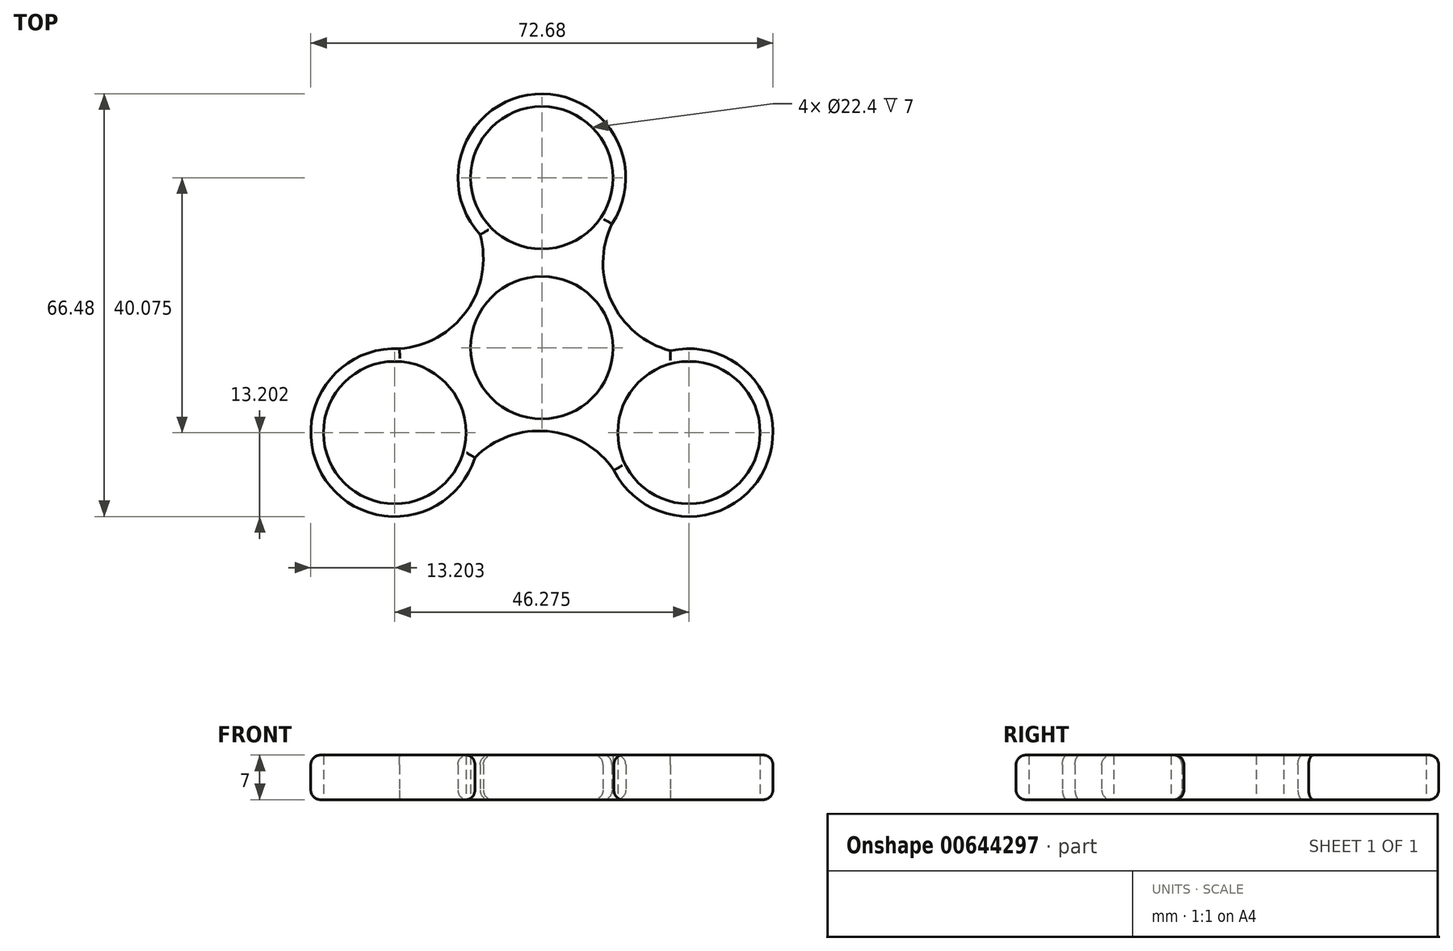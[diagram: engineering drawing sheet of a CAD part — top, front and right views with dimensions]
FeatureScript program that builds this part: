
annotation { "Feature Type Name" : "Feature", "Feature Type Description" : "" }
export const myFeature = defineFeature(function(context is Context, id is Id, definition is map)
    precondition{}
    {
        {
            var Q0;
            Q0=qCreatedBy(makeId("Top.planeOp"),FACE);
            var sketch = newSketch(context, id + "F0", { "sketchPlane" : qUnion([Q0])});
            skCircle(sketch, "E0", {"center": v(0, 0) * mm, "radius": 11.2 * mm});
            skArc(sketch, "E1", {"start": v(-10.62, 7.84) * mm, "mid": v(-11.33, 6.77) * mm, "end": v(-11.93, 5.65) * mm});
            skCircle(sketch, "E2", {"center": v(0, 26.72) * mm, "radius": 11.2 * mm});
            skArc(sketch, "E3", {"start": v(11.03, 19.46) * mm, "mid": v(-1.07, 39.87) * mm, "end": v(-9.7, 17.77) * mm});
            skCircle(sketch, "E4.1.0", {"center": v(-23.14, -13.36) * mm, "radius": 11.2 * mm});
            skArc(sketch, "E4.1.1", {"start": v(-22.36, -0.18) * mm, "mid": v(-34, -20.86) * mm, "end": v(-10.54, -17.3) * mm});
            skCircle(sketch, "E4.2.0", {"center": v(23.14, -13.36) * mm, "radius": 11.2 * mm});
            skArc(sketch, "E4.2.1", {"start": v(11.34, -19.28) * mm, "mid": v(35.07, -19) * mm, "end": v(20.24, -0.48) * mm});
            skArc(sketch, "E5", {"start": v(11.03, 19.46) * mm, "mid": v(10.94, 7.32) * mm, "end": v(20.24, -0.48) * mm});
            skArc(sketch, "E6.1.0", {"start": v(-22.36, -0.18) * mm, "mid": v(-11.8, 5.82) * mm, "end": v(-9.7, 17.77) * mm});
            skArc(sketch, "E6.2.0", {"start": v(11.34, -19.28) * mm, "mid": v(0.87, -13.14) * mm, "end": v(-10.54, -17.3) * mm});
            skArc(sketch, "E7.trimOffspring", {"start": v(12.1, 5.28) * mm, "mid": v(11.53, 6.42) * mm, "end": v(10.86, 7.5) * mm});
            skArc(sketch, "E8.trimOffspring", {"start": v(-1.48, -13.12) * mm, "mid": v(-0.2, -13.2) * mm, "end": v(1.08, -13.16) * mm});
            skLineSegment(sketch, "E9", {"start": v(-48.96, -28.96) * mm, "end": v(42.62, -28.96) * mm, "construction": true});
            skSolve(sketch);
        }
        {
            var Q0;
            Q0=makeQuery(id+"F0.imprint","IMPRINT",FACE,{"disambiguationData":[TD([[makeQuery(id+"F0.imprint","IMPRINT",EDGE,{"derivedFrom":sQuery(id+"F0.wireOp",EDGE,"E0")}),-1.0]])]});
            extrude(context, id + "F1", {"entities" : qUnion([Q0]), "depth" : 7 * mm, "offsetDistance" : 25 * mm});
        }
        {
            var Q0;
            Q0=makeQuery(id+"F1.opExtrude","CAP_EDGE",EDGE,{"disambiguationData":[OSD([sQuery(id+"F0.wireOp",EDGE,"E4.2.1")])],"isStart":false});
            var Q1;
            Q1=makeQuery(id+"F1.opExtrude","CAP_EDGE",EDGE,{"disambiguationData":[OSD([sQuery(id+"F0.wireOp",EDGE,"E5")])],"isStart":false});
            var Q2;
            Q2=makeQuery(id+"F1.opExtrude","CAP_EDGE",EDGE,{"disambiguationData":[OSD([sQuery(id+"F0.wireOp",EDGE,"E6.2.0")])],"isStart":false});
            var Q3;
            Q3=makeQuery(id+"F1.opExtrude","CAP_EDGE",EDGE,{"disambiguationData":[OSD([sQuery(id+"F0.wireOp",EDGE,"E4.1.1")])],"isStart":false});
            var Q4;
            Q4=makeQuery(id+"F1.opExtrude","CAP_EDGE",EDGE,{"disambiguationData":[OSD([sQuery(id+"F0.wireOp",EDGE,"E6.1.0")])],"isStart":false});
            var Q5;
            Q5=makeQuery(id+"F1.opExtrude","CAP_EDGE",EDGE,{"disambiguationData":[OSD([sQuery(id+"F0.wireOp",EDGE,"E3")])],"isStart":false});
            fillet(context, id + "F2", {"entities" : qUnion([Q0, Q1, Q2, Q3, Q4, Q5]), "tangentPropagation" : true, "radius" : 1.5 * mm, "defaultsChanged" : false, "vertexSettings" : [], "allowEdgeOverflow" : false});
        }
        {
            var Q0;
            Q0=makeQuery(id+"F1.opExtrude","CAP_EDGE",EDGE,{"disambiguationData":[OSD([sQuery(id+"F0.wireOp",EDGE,"E4.2.1")])],"isStart":true});
            var Q1;
            Q1=makeQuery(id+"F1.opExtrude","CAP_EDGE",EDGE,{"disambiguationData":[OSD([sQuery(id+"F0.wireOp",EDGE,"E5")])],"isStart":true});
            var Q2;
            Q2=makeQuery(id+"F1.opExtrude","CAP_EDGE",EDGE,{"disambiguationData":[OSD([sQuery(id+"F0.wireOp",EDGE,"E6.2.0")])],"isStart":true});
            var Q3;
            Q3=makeQuery(id+"F1.opExtrude","CAP_EDGE",EDGE,{"disambiguationData":[OSD([sQuery(id+"F0.wireOp",EDGE,"E4.1.1")])],"isStart":true});
            var Q4;
            Q4=makeQuery(id+"F1.opExtrude","CAP_EDGE",EDGE,{"disambiguationData":[OSD([sQuery(id+"F0.wireOp",EDGE,"E6.1.0")])],"isStart":true});
            var Q5;
            Q5=makeQuery(id+"F1.opExtrude","CAP_EDGE",EDGE,{"disambiguationData":[OSD([sQuery(id+"F0.wireOp",EDGE,"E3")])],"isStart":true});
            fillet(context, id + "F3", {"entities" : qUnion([Q0, Q1, Q2, Q3, Q4, Q5]), "tangentPropagation" : true, "radius" : 1.5 * mm, "defaultsChanged" : true, "vertexSettings" : [], "allowEdgeOverflow" : false});
        }
    });
